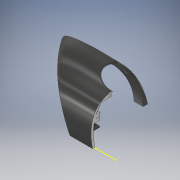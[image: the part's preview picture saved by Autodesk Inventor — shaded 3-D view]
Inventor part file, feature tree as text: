
AUTODESK INVENTOR PART (.ipt)
format: ipt  version: 2019 (Build 230136000, 136)  size: 1,266,688 bytes
history: native  units: mm
features: plane x27, sketch x24, extrude x11, fillet x6, mirror x5, loft x4, chamfer x3, other x1
ambient origin geometry x8: Origin, YZ Plane, XZ Plane, XY Plane, X Axis, Y Axis, Z Axis, Center Point
bodies: Body1 (feature_tree)
feature tree (81):
  sketch  "Sketch1"  dims[d2=55.0mm d5=-107.0mm d13=5.0mm d14=50.0mm]
  plane  "Work Plane1"
  sketch  "Sketch2"  dims[d15=70.0mm d16=5.0mm]
  sketch  "Sketch3"  dims[d17=0.0mm d18=90.0deg d19=0.0mm d20=90.0deg d21=0.0mm d22=90.0deg d23=2.0mm]
  plane  "Work Plane2"
  loft  "Loft2"
  mirror  "Mirror2"
  fillet  "Fillet1"  Radius=5.0mm
  fillet  "Fillet4"  Radius=50.0mm
  plane  "Work Plane3"
  plane  "Work Plane4"
  extrude  "Extrusion1"  Depth=5.0mm
  plane  "Work Plane5"
  extrude  "Extrusion2"  TaperAngle=0.0deg  [1 undecoded]
  fillet  "Fillet5"  [1 undecoded]
  mirror  "Mirror3"
  plane  "Work Plane22"
  plane  "Work Plane6"
  plane  "Work Plane7"
  fillet  "Fillet11"  Radius=2.0mm
  extrude  "Extrusion7"  Depth=87.5mm
  mirror  "Mirror4"
  plane  "Work Plane8"
  plane  "Work Plane9"
  sketch  "Sketch20"  dims[d42=2.0mm]
  plane  "Work Plane10"
  sketch  "Sketch21"  dims[d43=2.0mm]
  plane  "Work Plane11"
  sketch  "Sketch22"  dims[d44=2.0mm]
  loft  "Loft5"
  plane  "Work Plane13"
  sketch  "Sketch25"  dims[d45=2.0mm]
  plane  "Work Plane18"
  loft  "Loft6"
  mirror  "Mirror5"
  plane  "Work Plane19"
  extrude  "Extrusion9"  Depth=2.0mm
  fillet  "Fillet12"  Radius=2.0mm
  fillet  "Fillet14"  Radius=2.0mm
  plane  "Work Plane20"
  plane  "Work Plane21"
  plane  "Work Plane23"
  plane  "Work Plane24"
  plane  "Work Plane25"
  sketch  "Sketch33"  dims[d48=2.0mm]
  plane  "Work Plane26"
  sketch  "Sketch34"  dims[d49=2.0mm d50=2.0mm d51=1.0mm]
  plane  "Work Plane27"
  sketch  "Sketch35"  dims[d79=-25.0mm]
  plane  "Work Plane30"
  sketch  "Sketch38"  dims[d84=2.0mm]
  plane  "Work Plane31"
  plane  "Work Plane35"
  chamfer  "Chamfer7"  Distance=2.0mm
  chamfer  "Chamfer8"  Distance=28.0mm
  chamfer  "Chamfer9"  Distance=22.0mm
  loft  "Loft10"
  mirror  "Mirror9"
  plane  "Work Plane37"
  extrude  "Extrusion24"  Depth=70.0mm
  extrude  "Extrusion25"  Depth=3.0mm
  extrude  "Extrusion26"  Depth=20.0mm
  extrude  "Extrusion27"  TaperAngle=0.0deg  [1 undecoded]
  plane  "Work Plane38"
  extrude  "Extrusion28"  TaperAngle=0.0deg  [1 undecoded]
  extrude  "Extrusion29"  TaperAngle=0.0deg  [1 undecoded]
  extrude  "Extrusion30"  [1 undecoded]
  sketch  "Sketch4"  dims[d29=1.0mm d30=-4.5mm d31=87.5mm]
  sketch  "Sketch5"  dims[d32=0.0mm d33=0.0mm d34=-28.0mm]
  sketch  "Sketch6"  dims[d35=15.0mm d36=3.0mm]
  sketch  "Sketch17"  dims[d37=0.0mm d38=0.0mm d39=2.0mm d40=2.0mm d41=2.0mm]
  sketch  "Sketch27"  dims[d46=2.0mm]
  other  "Edges1"
  sketch  "Sketch28"  dims[d47=2.0mm]
  sketch  "Sketch47"  dims[d85=13.5mm]
  sketch  "Sketch48"  dims[d86=2.5mm]
  sketch  "Sketch49"  dims[d87=5.0mm]
  sketch  "Sketch50"  dims[d88=6.25mm d89=28.0mm d90=0.0mm d91=22.0mm d101=200.0mm]
  sketch  "Sketch51"  dims[d104=5.0mm d105=50.0mm d106=-80.0mm d107=45.0mm]
  sketch  "Sketch52"  dims[d108=3.0mm d109=70.0mm]
  sketch  "Sketch53"  dims[d110=80.0mm d111=3.0mm d112=20.0mm d123=0.0mm d124=90.0deg d125=0.0mm d126=90.0deg d127=0.0mm d128=90.0deg d129=-20.0mm d131=2.0mm d132=80.0mm d133=10.0mm d134=0.0mm d135=0.0mm d136=90.0deg d137=0.0mm d138=90.0deg d139=0.0mm d140=90.0deg d141=3.0mm d142=7.0mm d143=10.0mm d144=0.0mm d145=70.0mm d147=10.0mm d171=35.75mm d174=-8.25mm d177=20.0mm d179=30.0mm d180=5.0mm d181=41.5mm d182=15.0mm d183=10.0mm d184=5.0mm d200=-2.0mm d219=15.0mm d241=2.0mm d242=2.0mm d243=45.0deg d244=1.0mm d245=2.0mm d246=45.0deg d247=0.5mm d248=2.0mm d249=45.0deg d250=5.0mm d251=0.0mm d252=90.0deg d253=0.0mm d254=90.0deg d255=0.0mm d256=90.0deg d261=0.0mm d262=0.0mm d263=10.0mm d264=0.0mm d265=5.0mm d266=0.0mm d267=4.0mm d268=20.0mm d269=0.0mm d270=16.0mm d271=14.0mm d272=20.0mm d273=0.0mm d274=4.0mm d275=20.0mm d276=0.0mm d277=0.0mm d278=0.0mm]
note: 6 required parameter values undecoded (feature->parameter linkage not recoverable at this tier; creation-order binding heuristic only, values carry confidence <= 0.55)
